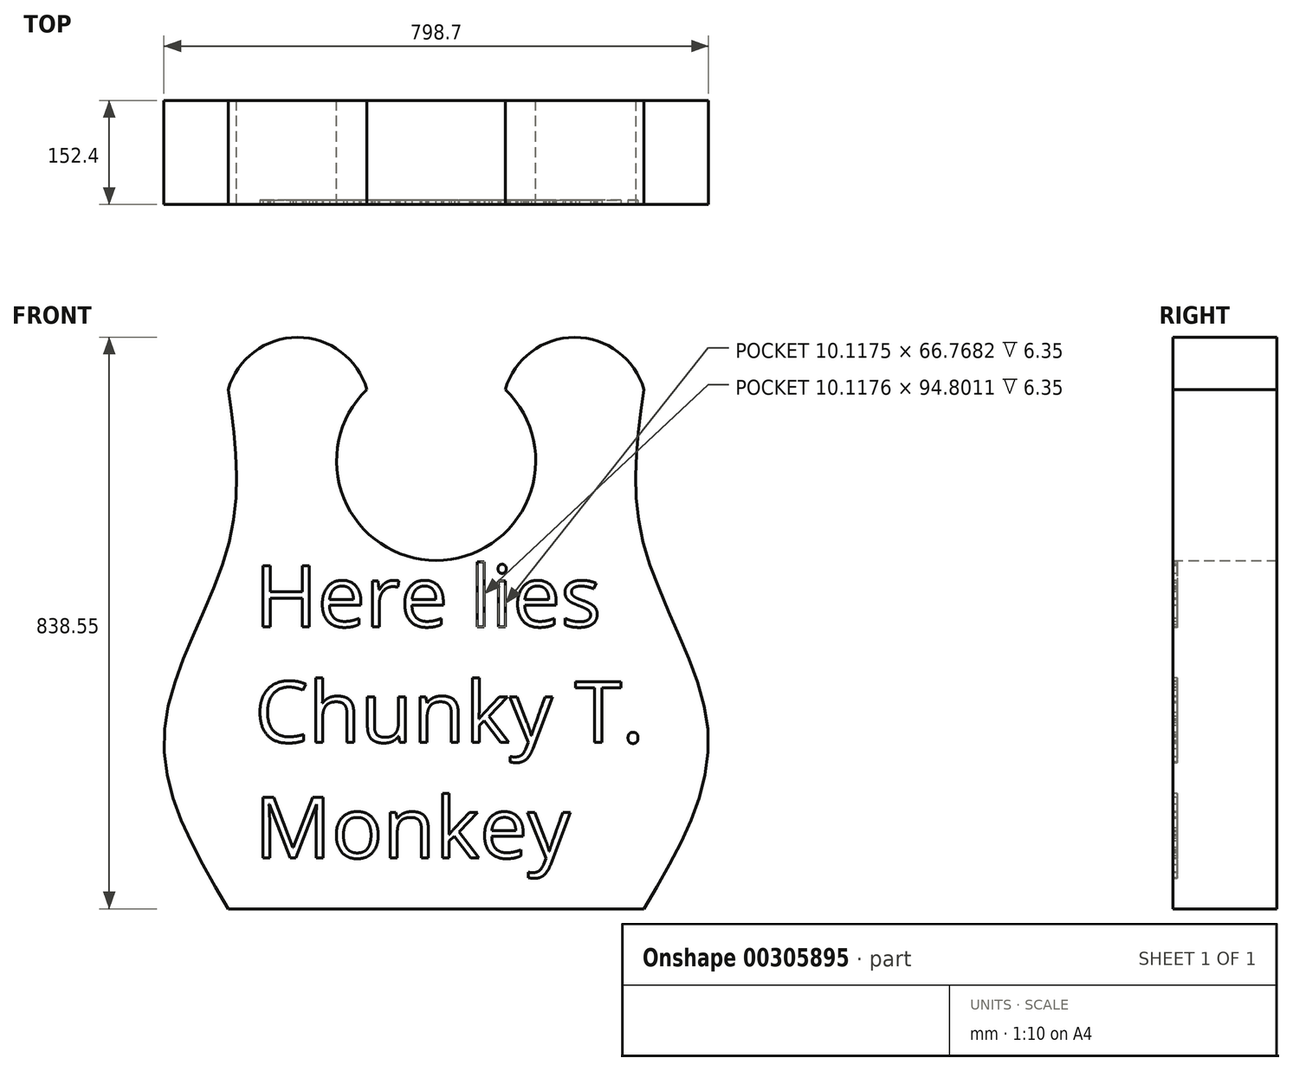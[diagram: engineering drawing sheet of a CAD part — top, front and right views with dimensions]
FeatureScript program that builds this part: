
annotation { "Feature Type Name" : "Feature", "Feature Type Description" : "" }
export const myFeature = defineFeature(function(context is Context, id is Id, definition is map)
    precondition{}
    {
        {
            var Q0;
            Q0=qCreatedBy(makeId("Front.planeOp"),FACE);
            var sketch = newSketch(context, id + "F0", { "sketchPlane" : qUnion([Q0])});
            skLineSegment(sketch, "E0", {"start": v(-482.82, 0) * mm, "end": v(126.78, 0) * mm});
            skArc(sketch, "E1", {"start": v(-279.62, 762) * mm, "mid": v(-381.22, 838.55) * mm, "end": v(-482.82, 762) * mm});
            skArc(sketch, "E2", {"start": v(126.78, 762) * mm, "mid": v(25.18, 838.55) * mm, "end": v(-76.42, 762) * mm});
            skArc(sketch, "E3", {"start": v(-279.62, 762) * mm, "mid": v(-178.02, 511.2) * mm, "end": v(-76.42, 762) * mm});
            skFitSpline(sketch, "E4", {"points": [v(-482.82, 762) * mm, v(-482.82, 532.91) * mm, v(-576.95, 256.96) * mm, v(-482.82, 0) * mm], "startDerivative": vector(102.65, -723.37) * mm, "endDerivative": vector(440.31, -745.74) * mm});
            skFitSpline(sketch, "E5.MirrorCS", {"points": [v(126.78, 762) * mm, v(126.78, 532.91) * mm, v(220.92, 256.96) * mm, v(126.78, 0) * mm], "startDerivative": vector(-102.65, -723.37) * mm, "endDerivative": vector(-440.31, -745.74) * mm});
            skSolve(sketch);
        }
        {
            var Q0;
            Q0=makeQuery(id+"F0.imprint","IMPRINT",FACE,{"disambiguationData":[TD([[makeQuery(id+"F0.imprint","IMPRINT",EDGE,{"derivedFrom":sQuery(id+"F0.wireOp",EDGE,"E0")}),1.0]])]});
            extrude(context, id + "F1", {"entities" : qUnion([Q0]), "depth" : 152.4 * mm});
        }
        {
            var Q0;
            Q0=makeQuery(id+"F1.opExtrude","CAP_FACE",FACE,{"disambiguationData":[OSD([sQuery(id+"F0.wireOp",EDGE,"E0"),sQuery(id+"F0.wireOp",EDGE,"E1"),sQuery(id+"F0.wireOp",EDGE,"E2"),sQuery(id+"F0.wireOp",EDGE,"E3"),sQuery(id+"F0.wireOp",EDGE,"E4"),sQuery(id+"F0.wireOp",EDGE,"E5.MirrorCS")])],"isStart":false});
            var sketch = newSketch(context, id + "F2", { "sketchPlane" : qUnion([Q0])});
            skText(sketch, "E6", { "text": "Here lies\nChunky T.\nMonkey", "fontName": "OpenSans-Regular.ttf"});
            const initialGuessF2  = {"E6": [-0.44405, 0.414, 1, 0, 0.08983]};
            skSetInitialGuess(sketch, initialGuessF2);
            skSolve(sketch);
        }
        {
            var Q0;
            Q0 = qSketchRegion(id + "F2", true);
            extrude(context, id + "F3", {"entities" : qUnion([Q0]), "operationType" : NewBodyOperationType.REMOVE, "oppositeDirection" : true, "depth" : 6.35 * mm});
        }
    });
